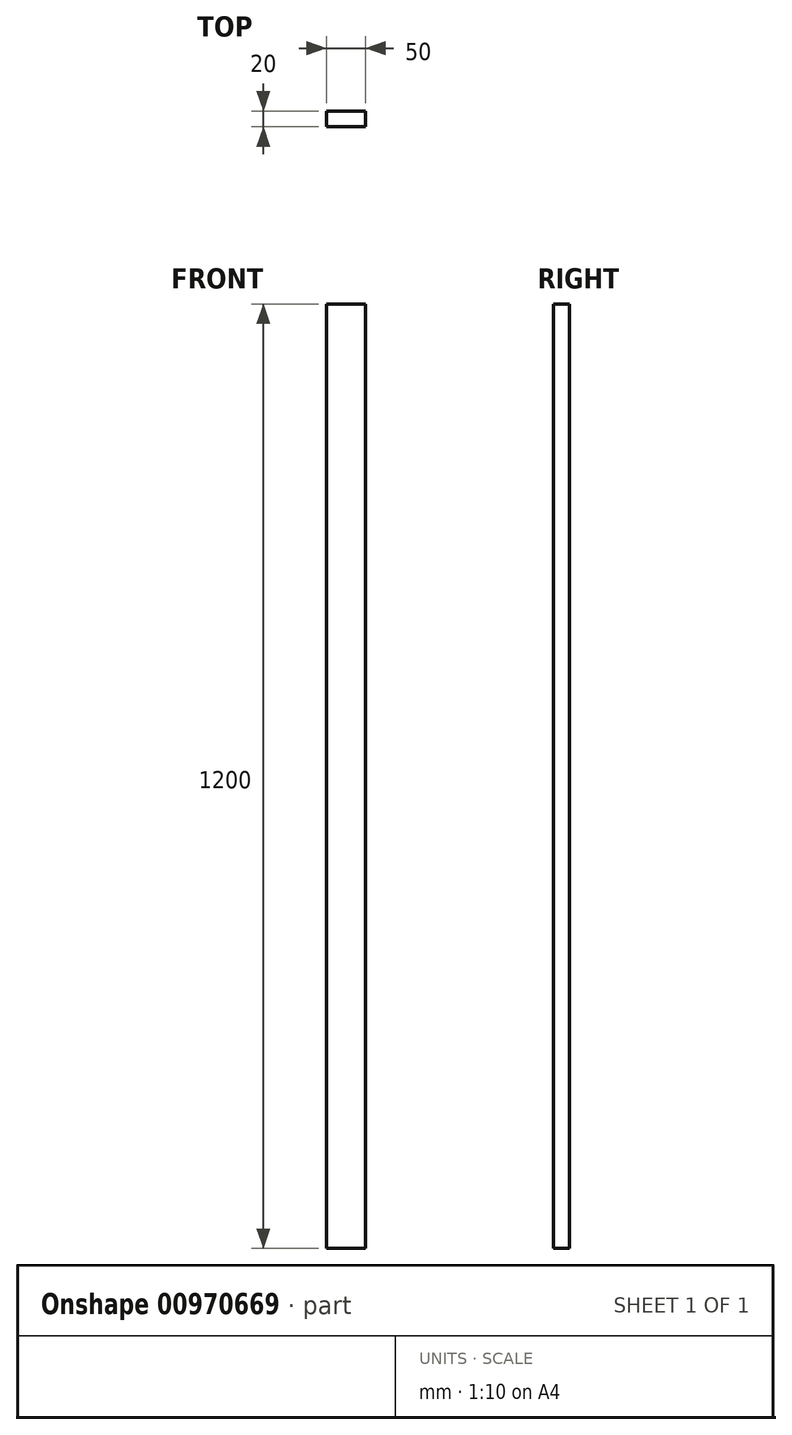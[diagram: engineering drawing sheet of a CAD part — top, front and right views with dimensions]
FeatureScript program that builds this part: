
annotation { "Feature Type Name" : "Feature", "Feature Type Description" : "" }
export const myFeature = defineFeature(function(context is Context, id is Id, definition is map)
    precondition{}
    {
        {
            var Q0;
            Q0=qCreatedBy(makeId("Top.planeOp"),FACE);
            var sketch = newSketch(context, id + "F0", { "sketchPlane" : qUnion([Q0])});
            skLineSegment(sketch, "E0.bottom", {"start": v(-32.35, -11.35) * mm, "end": v(17.65, -11.35) * mm});
            skLineSegment(sketch, "E0.top", {"start": v(-32.35, -31.35) * mm, "end": v(17.65, -31.35) * mm});
            skLineSegment(sketch, "E0.left", {"start": v(-32.35, -11.35) * mm, "end": v(-32.35, -31.35) * mm});
            skLineSegment(sketch, "E0.right", {"start": v(17.65, -11.35) * mm, "end": v(17.65, -31.35) * mm});
            skSolve(sketch);
        }
        {
            var Q0;
            Q0 = qSketchRegion(id + "F0", true);
            extrude(context, id + "F1", {"entities" : qUnion([Q0]), "depth" : 1200 * mm, "offsetDistance" : 25 * mm});
        }
    });
